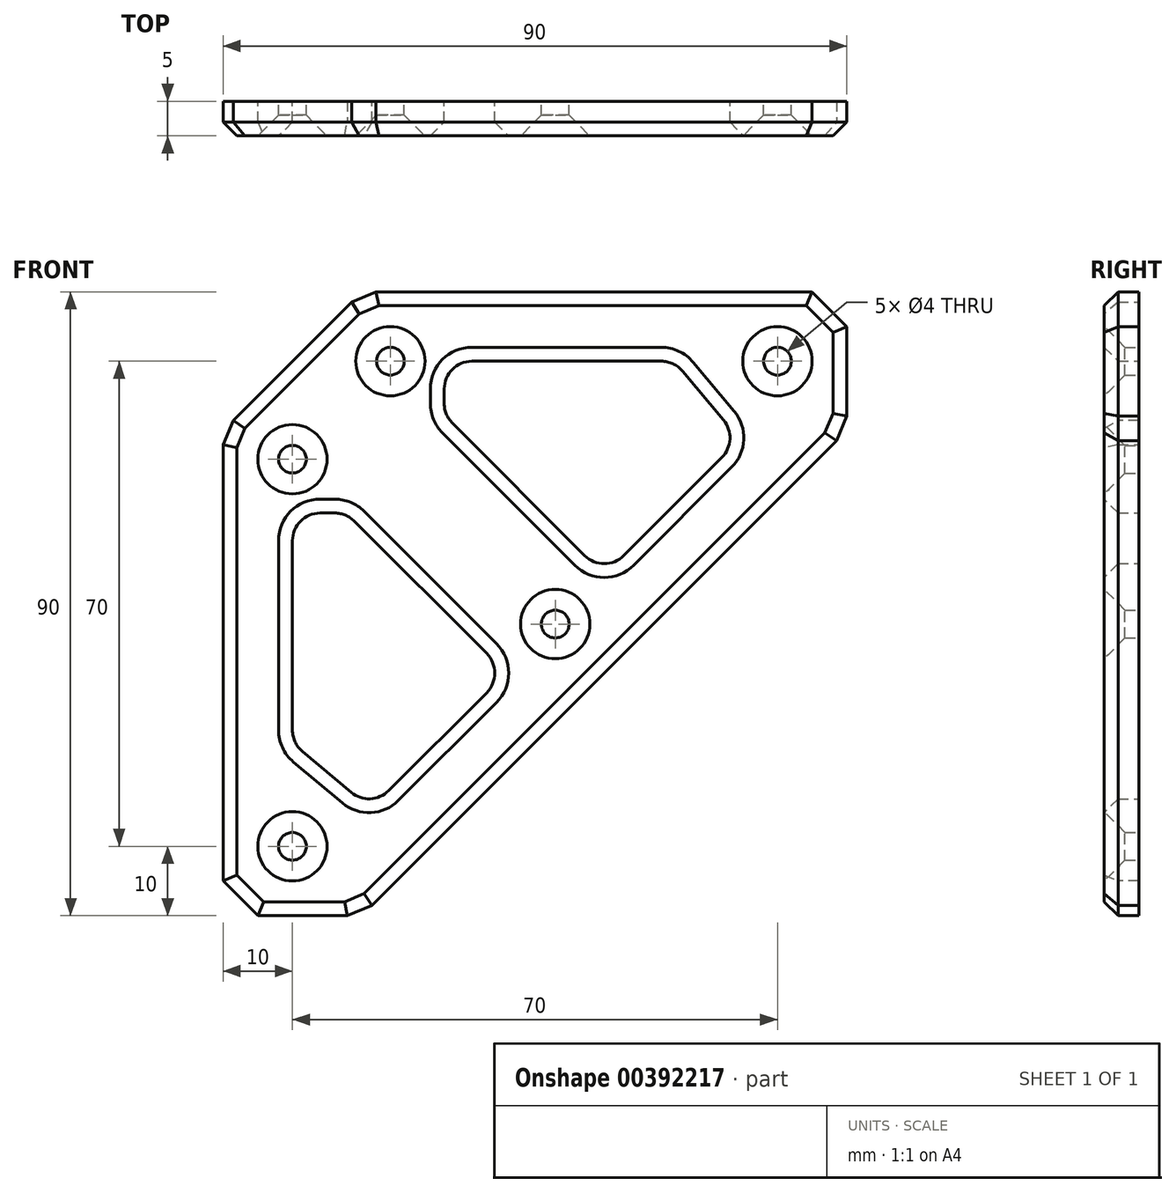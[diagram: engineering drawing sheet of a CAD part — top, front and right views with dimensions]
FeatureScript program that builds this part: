
annotation { "Feature Type Name" : "Feature", "Feature Type Description" : "" }
export const myFeature = defineFeature(function(context is Context, id is Id, definition is map)
    precondition{}
    {
        {
            var Q0;
            Q0=qCreatedBy(makeId("Front.planeOp"),FACE);
            var sketch = newSketch(context, id + "F0", { "sketchPlane" : qUnion([Q0])});
            skLineSegment(sketch, "E0", {"start": v(0, -20) * mm, "end": v(20, 0) * mm});
            skLineSegment(sketch, "E1", {"start": v(20, 0) * mm, "end": v(90, 0) * mm});
            skLineSegment(sketch, "E2", {"start": v(90, 0) * mm, "end": v(90, -20) * mm});
            skLineSegment(sketch, "E3", {"start": v(90, -20) * mm, "end": v(20, -90) * mm});
            skLineSegment(sketch, "E4", {"start": v(20, -90) * mm, "end": v(0, -90) * mm});
            skLineSegment(sketch, "E5", {"start": v(0, -90) * mm, "end": v(0, -20) * mm});
            skLineSegment(sketch, "E6.0", {"start": v(10, -24.14) * mm, "end": v(24.14, -10) * mm, "construction": true});
            skLineSegment(sketch, "E6.1", {"start": v(80, -10) * mm, "end": v(80, -15.86) * mm, "construction": true});
            skLineSegment(sketch, "E6.2", {"start": v(80, -15.86) * mm, "end": v(15.86, -80) * mm, "construction": true});
            skLineSegment(sketch, "E6.3", {"start": v(24.14, -10) * mm, "end": v(80, -10) * mm, "construction": true});
            skLineSegment(sketch, "E6.4", {"start": v(15.86, -80) * mm, "end": v(10, -80) * mm, "construction": true});
            skLineSegment(sketch, "E6.5", {"start": v(10, -80) * mm, "end": v(10, -24.14) * mm, "construction": true});
            skLineSegment(sketch, "E7", {"start": v(0, 0) * mm, "end": v(55, -55) * mm, "construction": true});
            skPoint(sketch, "E8", {"position": v(47.93, -47.93) * mm});
            skCircle(sketch, "E9", {"center": v(10, -24.14) * mm, "radius": 2 * mm});
            skCircle(sketch, "E10", {"center": v(24.14, -10) * mm, "radius": 2 * mm});
            skCircle(sketch, "E11", {"center": v(80, -10) * mm, "radius": 2 * mm});
            skCircle(sketch, "E12", {"center": v(47.93, -47.93) * mm, "radius": 2 * mm});
            skCircle(sketch, "E13", {"center": v(10, -80) * mm, "radius": 2 * mm});
            skLineSegment(sketch, "E14", {"start": v(66.28, -11.43) * mm, "end": v(72.2, -18.49) * mm});
            skLineSegment(sketch, "E15", {"start": v(71.97, -23.89) * mm, "end": v(57.83, -38.03) * mm});
            skLineSegment(sketch, "E16", {"start": v(52.17, -38.03) * mm, "end": v(33.08, -18.94) * mm});
            skLineSegment(sketch, "E17", {"start": v(31.9, -16.1) * mm, "end": v(31.9, -14) * mm});
            skLineSegment(sketch, "E18", {"start": v(35.9, -10) * mm, "end": v(63.22, -10) * mm});
            skPoint(sketch, "E19.visualSharp", {"position": v(55, -40.86) * mm});
            skArc(sketch, "E19.filletArc", {"start": v(52.17, -38.03) * mm, "mid": v(55, -39.2) * mm, "end": v(57.83, -38.03) * mm});
            skPoint(sketch, "E20.visualSharp", {"position": v(31.9, -17.77) * mm});
            skArc(sketch, "E20.filletArc", {"start": v(31.9, -16.1) * mm, "mid": v(32.21, -17.64) * mm, "end": v(33.08, -18.94) * mm});
            skPoint(sketch, "E21.visualSharp", {"position": v(31.9, -10) * mm});
            skArc(sketch, "E21.filletArc", {"start": v(35.9, -10) * mm, "mid": v(33.08, -11.17) * mm, "end": v(31.9, -14) * mm});
            skPoint(sketch, "E22.visualSharp", {"position": v(65.08, -10) * mm});
            skArc(sketch, "E22.filletArc", {"start": v(66.28, -11.43) * mm, "mid": v(64.9, -10.37) * mm, "end": v(63.22, -10) * mm});
            skPoint(sketch, "E23.visualSharp", {"position": v(74.56, -21.3) * mm});
            skArc(sketch, "E23.filletArc", {"start": v(71.97, -23.89) * mm, "mid": v(73.14, -21.23) * mm, "end": v(72.2, -18.49) * mm});
            skLineSegment(sketch, "E24.MirrorCS", {"start": v(16.1, -31.9) * mm, "end": v(14, -31.9) * mm});
            skArc(sketch, "E25.MirrorCS", {"start": v(16.1, -31.9) * mm, "mid": v(17.64, -32.21) * mm, "end": v(18.94, -33.08) * mm});
            skArc(sketch, "E26.MirrorCS", {"start": v(10, -35.9) * mm, "mid": v(11.17, -33.08) * mm, "end": v(14, -31.9) * mm});
            skPoint(sketch, "E27.MirrorP", {"position": v(17.77, -31.9) * mm});
            skPoint(sketch, "E28.MirrorP", {"position": v(10, -31.9) * mm});
            skPoint(sketch, "E29.MirrorP", {"position": v(40.86, -55) * mm});
            skArc(sketch, "E30.MirrorCS", {"start": v(38.03, -52.17) * mm, "mid": v(39.2, -55) * mm, "end": v(38.03, -57.83) * mm});
            skArc(sketch, "E31.MirrorCS", {"start": v(11.43, -66.28) * mm, "mid": v(10.37, -64.9) * mm, "end": v(10, -63.22) * mm});
            skPoint(sketch, "E32.MirrorP", {"position": v(10, -65.08) * mm});
            skArc(sketch, "E33.MirrorCS", {"start": v(23.89, -71.97) * mm, "mid": v(21.23, -73.14) * mm, "end": v(18.49, -72.2) * mm});
            skPoint(sketch, "E34.MirrorP", {"position": v(21.3, -74.56) * mm});
            skLineSegment(sketch, "E35.MirrorCS", {"start": v(11.43, -66.28) * mm, "end": v(18.49, -72.2) * mm});
            skLineSegment(sketch, "E36.MirrorCS", {"start": v(10, -35.9) * mm, "end": v(10, -63.22) * mm});
            skLineSegment(sketch, "E37.MirrorCS", {"start": v(38.03, -52.17) * mm, "end": v(18.94, -33.08) * mm});
            skLineSegment(sketch, "E38.MirrorCS", {"start": v(23.89, -71.97) * mm, "end": v(38.03, -57.83) * mm});
            skSolve(sketch);
        }
        {
            var Q0;
            Q0=qSketchRegion(id+"F0",true);
            extrude(context, id + "F1", {"entities" : qUnion([Q0]), "depth" : 5 * mm});
        }
        {
            var Q0;
            Q0=makeQuery(id+"F1.opExtrude","SWEPT_EDGE",EDGE,{"disambiguationData":[OSD([sQuery(id+"F0.wireOp",EDGE,"E1"),sQuery(id+"F0.wireOp",EDGE,"E2")])]});
            var Q1;
            Q1=makeQuery(id+"F1.opExtrude","SWEPT_EDGE",EDGE,{"disambiguationData":[OSD([sQuery(id+"F0.wireOp",EDGE,"E4"),sQuery(id+"F0.wireOp",EDGE,"E5")])]});
            var Q2;
            Q2=makeQuery(id+"F1.opExtrude","SWEPT_EDGE",EDGE,{"disambiguationData":[OSD([sQuery(id+"F0.wireOp",EDGE,"E0"),sQuery(id+"F0.wireOp",EDGE,"E5")])]});
            var Q3;
            Q3=makeQuery(id+"F1.opExtrude","SWEPT_EDGE",EDGE,{"disambiguationData":[OSD([sQuery(id+"F0.wireOp",EDGE,"E0"),sQuery(id+"F0.wireOp",EDGE,"E1")])]});
            var Q4;
            Q4=makeQuery(id+"F1.opExtrude","SWEPT_EDGE",EDGE,{"disambiguationData":[OSD([sQuery(id+"F0.wireOp",EDGE,"E2"),sQuery(id+"F0.wireOp",EDGE,"E3")])]});
            var Q5;
            Q5=makeQuery(id+"F1.opExtrude","SWEPT_EDGE",EDGE,{"disambiguationData":[OSD([sQuery(id+"F0.wireOp",EDGE,"E3"),sQuery(id+"F0.wireOp",EDGE,"E4")])]});
            chamfer(context, id + "F2", {"entities" : qUnion([Q0, Q1, Q2, Q3, Q4, Q5]), "width" : 5 * mm, "tangentPropagation" : true});
        }
        {
            var Q0;
            {var subQ0=sQuery(id+"F0.wireOp",EDGE,"E5");var subQ1=sQuery(id+"F0.wireOp",EDGE,"E0");Q0=makeQuery(id+"F2.opChamfer","BLEND_EDGE",EDGE,{"blendedFrom":[makeQuery(id+"F1.opExtrude","SWEPT_EDGE",EDGE,{"disambiguationData":[OSD([subQ1,subQ0])]}),makeQuery(id+"F1.opExtrude","CAP_FACE",FACE,{"disambiguationData":[OSD([subQ1,sQuery(id+"F0.wireOp",EDGE,"E1"),sQuery(id+"F0.wireOp",EDGE,"E2"),sQuery(id+"F0.wireOp",EDGE,"E3"),sQuery(id+"F0.wireOp",EDGE,"E4"),subQ0,sQuery(id+"F0.wireOp",EDGE,"E9"),sQuery(id+"F0.wireOp",EDGE,"E10"),sQuery(id+"F0.wireOp",EDGE,"E11"),sQuery(id+"F0.wireOp",EDGE,"E12"),sQuery(id+"F0.wireOp",EDGE,"E13")])],"isStart":false})],"blendedInto":[makeQuery(id+"F1.opExtrude","CAP_FACE",FACE,{"disambiguationData":[OSD([subQ1,sQuery(id+"F0.wireOp",EDGE,"E1"),sQuery(id+"F0.wireOp",EDGE,"E2"),sQuery(id+"F0.wireOp",EDGE,"E3"),sQuery(id+"F0.wireOp",EDGE,"E4"),subQ0,sQuery(id+"F0.wireOp",EDGE,"E9"),sQuery(id+"F0.wireOp",EDGE,"E10"),sQuery(id+"F0.wireOp",EDGE,"E11"),sQuery(id+"F0.wireOp",EDGE,"E12"),sQuery(id+"F0.wireOp",EDGE,"E13")])],"isStart":false})]});}
            var Q1;
            {var subQ0=sQuery(id+"F0.wireOp",EDGE,"E1");var subQ1=sQuery(id+"F0.wireOp",EDGE,"E0");Q1=makeQuery(id+"F2.opChamfer","BLEND_EDGE",EDGE,{"blendedFrom":[makeQuery(id+"F1.opExtrude","SWEPT_EDGE",EDGE,{"disambiguationData":[OSD([subQ1,subQ0])]}),makeQuery(id+"F1.opExtrude","CAP_FACE",FACE,{"disambiguationData":[OSD([subQ1,subQ0,sQuery(id+"F0.wireOp",EDGE,"E2"),sQuery(id+"F0.wireOp",EDGE,"E3"),sQuery(id+"F0.wireOp",EDGE,"E4"),sQuery(id+"F0.wireOp",EDGE,"E5"),sQuery(id+"F0.wireOp",EDGE,"E9"),sQuery(id+"F0.wireOp",EDGE,"E10"),sQuery(id+"F0.wireOp",EDGE,"E11"),sQuery(id+"F0.wireOp",EDGE,"E12"),sQuery(id+"F0.wireOp",EDGE,"E13")])],"isStart":false})],"blendedInto":[makeQuery(id+"F1.opExtrude","CAP_FACE",FACE,{"disambiguationData":[OSD([subQ1,subQ0,sQuery(id+"F0.wireOp",EDGE,"E2"),sQuery(id+"F0.wireOp",EDGE,"E3"),sQuery(id+"F0.wireOp",EDGE,"E4"),sQuery(id+"F0.wireOp",EDGE,"E5"),sQuery(id+"F0.wireOp",EDGE,"E9"),sQuery(id+"F0.wireOp",EDGE,"E10"),sQuery(id+"F0.wireOp",EDGE,"E11"),sQuery(id+"F0.wireOp",EDGE,"E12"),sQuery(id+"F0.wireOp",EDGE,"E13")])],"isStart":false})]});}
            var Q2;
            Q2=makeQuery(id+"F1.opExtrude","CAP_EDGE",EDGE,{"disambiguationData":[OSD([sQuery(id+"F0.wireOp",EDGE,"E0")])],"isStart":false});
            var Q3;
            {var subQ0=sQuery(id+"F0.wireOp",EDGE,"E2");var subQ1=sQuery(id+"F0.wireOp",EDGE,"E1");Q3=makeQuery(id+"F2.opChamfer","BLEND_EDGE",EDGE,{"blendedFrom":[makeQuery(id+"F1.opExtrude","SWEPT_EDGE",EDGE,{"disambiguationData":[OSD([subQ1,subQ0])]}),makeQuery(id+"F1.opExtrude","CAP_FACE",FACE,{"disambiguationData":[OSD([sQuery(id+"F0.wireOp",EDGE,"E0"),subQ1,subQ0,sQuery(id+"F0.wireOp",EDGE,"E3"),sQuery(id+"F0.wireOp",EDGE,"E4"),sQuery(id+"F0.wireOp",EDGE,"E5"),sQuery(id+"F0.wireOp",EDGE,"E9"),sQuery(id+"F0.wireOp",EDGE,"E10"),sQuery(id+"F0.wireOp",EDGE,"E11"),sQuery(id+"F0.wireOp",EDGE,"E12"),sQuery(id+"F0.wireOp",EDGE,"E13")])],"isStart":false})],"blendedInto":[makeQuery(id+"F1.opExtrude","CAP_FACE",FACE,{"disambiguationData":[OSD([sQuery(id+"F0.wireOp",EDGE,"E0"),subQ1,subQ0,sQuery(id+"F0.wireOp",EDGE,"E3"),sQuery(id+"F0.wireOp",EDGE,"E4"),sQuery(id+"F0.wireOp",EDGE,"E5"),sQuery(id+"F0.wireOp",EDGE,"E9"),sQuery(id+"F0.wireOp",EDGE,"E10"),sQuery(id+"F0.wireOp",EDGE,"E11"),sQuery(id+"F0.wireOp",EDGE,"E12"),sQuery(id+"F0.wireOp",EDGE,"E13")])],"isStart":false})]});}
            var Q4;
            {var subQ0=sQuery(id+"F0.wireOp",EDGE,"E3");var subQ1=sQuery(id+"F0.wireOp",EDGE,"E2");Q4=makeQuery(id+"F2.opChamfer","BLEND_EDGE",EDGE,{"blendedFrom":[makeQuery(id+"F1.opExtrude","SWEPT_EDGE",EDGE,{"disambiguationData":[OSD([subQ1,subQ0])]}),makeQuery(id+"F1.opExtrude","CAP_FACE",FACE,{"disambiguationData":[OSD([sQuery(id+"F0.wireOp",EDGE,"E0"),sQuery(id+"F0.wireOp",EDGE,"E1"),subQ1,subQ0,sQuery(id+"F0.wireOp",EDGE,"E4"),sQuery(id+"F0.wireOp",EDGE,"E5"),sQuery(id+"F0.wireOp",EDGE,"E9"),sQuery(id+"F0.wireOp",EDGE,"E10"),sQuery(id+"F0.wireOp",EDGE,"E11"),sQuery(id+"F0.wireOp",EDGE,"E12"),sQuery(id+"F0.wireOp",EDGE,"E13")])],"isStart":false})],"blendedInto":[makeQuery(id+"F1.opExtrude","CAP_FACE",FACE,{"disambiguationData":[OSD([sQuery(id+"F0.wireOp",EDGE,"E0"),sQuery(id+"F0.wireOp",EDGE,"E1"),subQ1,subQ0,sQuery(id+"F0.wireOp",EDGE,"E4"),sQuery(id+"F0.wireOp",EDGE,"E5"),sQuery(id+"F0.wireOp",EDGE,"E9"),sQuery(id+"F0.wireOp",EDGE,"E10"),sQuery(id+"F0.wireOp",EDGE,"E11"),sQuery(id+"F0.wireOp",EDGE,"E12"),sQuery(id+"F0.wireOp",EDGE,"E13")])],"isStart":false})]});}
            var Q5;
            Q5=makeQuery(id+"F1.opExtrude","CAP_EDGE",EDGE,{"disambiguationData":[OSD([sQuery(id+"F0.wireOp",EDGE,"E2")])],"isStart":false});
            var Q6;
            Q6=makeQuery(id+"F1.opExtrude","CAP_EDGE",EDGE,{"disambiguationData":[OSD([sQuery(id+"F0.wireOp",EDGE,"E1")])],"isStart":false});
            var Q7;
            {var subQ0=sQuery(id+"F0.wireOp",EDGE,"E4");var subQ1=sQuery(id+"F0.wireOp",EDGE,"E3");Q7=makeQuery(id+"F2.opChamfer","BLEND_EDGE",EDGE,{"blendedFrom":[makeQuery(id+"F1.opExtrude","SWEPT_EDGE",EDGE,{"disambiguationData":[OSD([subQ1,subQ0])]}),makeQuery(id+"F1.opExtrude","CAP_FACE",FACE,{"disambiguationData":[OSD([sQuery(id+"F0.wireOp",EDGE,"E0"),sQuery(id+"F0.wireOp",EDGE,"E1"),sQuery(id+"F0.wireOp",EDGE,"E2"),subQ1,subQ0,sQuery(id+"F0.wireOp",EDGE,"E5"),sQuery(id+"F0.wireOp",EDGE,"E9"),sQuery(id+"F0.wireOp",EDGE,"E10"),sQuery(id+"F0.wireOp",EDGE,"E11"),sQuery(id+"F0.wireOp",EDGE,"E12"),sQuery(id+"F0.wireOp",EDGE,"E13")])],"isStart":false})],"blendedInto":[makeQuery(id+"F1.opExtrude","CAP_FACE",FACE,{"disambiguationData":[OSD([sQuery(id+"F0.wireOp",EDGE,"E0"),sQuery(id+"F0.wireOp",EDGE,"E1"),sQuery(id+"F0.wireOp",EDGE,"E2"),subQ1,subQ0,sQuery(id+"F0.wireOp",EDGE,"E5"),sQuery(id+"F0.wireOp",EDGE,"E9"),sQuery(id+"F0.wireOp",EDGE,"E10"),sQuery(id+"F0.wireOp",EDGE,"E11"),sQuery(id+"F0.wireOp",EDGE,"E12"),sQuery(id+"F0.wireOp",EDGE,"E13")])],"isStart":false})]});}
            var Q8;
            {var subQ0=sQuery(id+"F0.wireOp",EDGE,"E5");var subQ1=sQuery(id+"F0.wireOp",EDGE,"E4");Q8=makeQuery(id+"F2.opChamfer","BLEND_EDGE",EDGE,{"blendedFrom":[makeQuery(id+"F1.opExtrude","SWEPT_EDGE",EDGE,{"disambiguationData":[OSD([subQ1,subQ0])]}),makeQuery(id+"F1.opExtrude","CAP_FACE",FACE,{"disambiguationData":[OSD([sQuery(id+"F0.wireOp",EDGE,"E0"),sQuery(id+"F0.wireOp",EDGE,"E1"),sQuery(id+"F0.wireOp",EDGE,"E2"),sQuery(id+"F0.wireOp",EDGE,"E3"),subQ1,subQ0,sQuery(id+"F0.wireOp",EDGE,"E9"),sQuery(id+"F0.wireOp",EDGE,"E10"),sQuery(id+"F0.wireOp",EDGE,"E11"),sQuery(id+"F0.wireOp",EDGE,"E12"),sQuery(id+"F0.wireOp",EDGE,"E13")])],"isStart":false})],"blendedInto":[makeQuery(id+"F1.opExtrude","CAP_FACE",FACE,{"disambiguationData":[OSD([sQuery(id+"F0.wireOp",EDGE,"E0"),sQuery(id+"F0.wireOp",EDGE,"E1"),sQuery(id+"F0.wireOp",EDGE,"E2"),sQuery(id+"F0.wireOp",EDGE,"E3"),subQ1,subQ0,sQuery(id+"F0.wireOp",EDGE,"E9"),sQuery(id+"F0.wireOp",EDGE,"E10"),sQuery(id+"F0.wireOp",EDGE,"E11"),sQuery(id+"F0.wireOp",EDGE,"E12"),sQuery(id+"F0.wireOp",EDGE,"E13")])],"isStart":false})]});}
            var Q9;
            Q9=makeQuery(id+"F1.opExtrude","CAP_EDGE",EDGE,{"disambiguationData":[OSD([sQuery(id+"F0.wireOp",EDGE,"E4")])],"isStart":false});
            var Q10;
            Q10=makeQuery(id+"F1.opExtrude","CAP_EDGE",EDGE,{"disambiguationData":[OSD([sQuery(id+"F0.wireOp",EDGE,"E5")])],"isStart":false});
            var Q11;
            Q11=makeQuery(id+"F1.opExtrude","CAP_EDGE",EDGE,{"disambiguationData":[OSD([sQuery(id+"F0.wireOp",EDGE,"E3")])],"isStart":false});
            chamfer(context, id + "F3", {"entities" : qUnion([Q0, Q1, Q2, Q3, Q4, Q5, Q6, Q7, Q8, Q9, Q10, Q11]), "width" : 2 * mm, "tangentPropagation" : true});
        }
        {
            var Q0;
            Q0=makeQuery(id+"F1.opExtrude","CAP_EDGE",EDGE,{"disambiguationData":[OSD([sQuery(id+"F0.wireOp",EDGE,"E9")])],"isStart":false});
            var Q1;
            Q1=makeQuery(id+"F1.opExtrude","CAP_EDGE",EDGE,{"disambiguationData":[OSD([sQuery(id+"F0.wireOp",EDGE,"E10")])],"isStart":false});
            var Q2;
            Q2=makeQuery(id+"F1.opExtrude","CAP_EDGE",EDGE,{"disambiguationData":[OSD([sQuery(id+"F0.wireOp",EDGE,"E11")])],"isStart":false});
            var Q3;
            Q3=makeQuery(id+"F1.opExtrude","CAP_EDGE",EDGE,{"disambiguationData":[OSD([sQuery(id+"F0.wireOp",EDGE,"E12")])],"isStart":false});
            var Q4;
            Q4=makeQuery(id+"F1.opExtrude","CAP_EDGE",EDGE,{"disambiguationData":[OSD([sQuery(id+"F0.wireOp",EDGE,"E13")])],"isStart":false});
            chamfer(context, id + "F4", {"entities" : qUnion([Q0, Q1, Q2, Q3, Q4]), "width" : 3 * mm, "tangentPropagation" : true});
        }
        {
            var Q0;
            Q0=makeQuery(id+"F1.opExtrude","CAP_EDGE",EDGE,{"disambiguationData":[OSD([sQuery(id+"F0.wireOp",EDGE,"E38.MirrorCS")])],"isStart":false});
            var Q1;
            Q1=makeQuery(id+"F1.opExtrude","CAP_EDGE",EDGE,{"disambiguationData":[OSD([sQuery(id+"F0.wireOp",EDGE,"E33.MirrorCS")])],"isStart":false});
            var Q2;
            Q2=makeQuery(id+"F1.opExtrude","CAP_EDGE",EDGE,{"disambiguationData":[OSD([sQuery(id+"F0.wireOp",EDGE,"E35.MirrorCS")])],"isStart":false});
            var Q3;
            Q3=makeQuery(id+"F1.opExtrude","CAP_EDGE",EDGE,{"disambiguationData":[OSD([sQuery(id+"F0.wireOp",EDGE,"E31.MirrorCS")])],"isStart":false});
            var Q4;
            Q4=makeQuery(id+"F1.opExtrude","CAP_EDGE",EDGE,{"disambiguationData":[OSD([sQuery(id+"F0.wireOp",EDGE,"E36.MirrorCS")])],"isStart":false});
            var Q5;
            Q5=makeQuery(id+"F1.opExtrude","CAP_EDGE",EDGE,{"disambiguationData":[OSD([sQuery(id+"F0.wireOp",EDGE,"E26.MirrorCS")])],"isStart":false});
            var Q6;
            Q6=makeQuery(id+"F1.opExtrude","CAP_EDGE",EDGE,{"disambiguationData":[OSD([sQuery(id+"F0.wireOp",EDGE,"E25.MirrorCS")])],"isStart":false});
            var Q7;
            Q7=makeQuery(id+"F1.opExtrude","SWEPT_EDGE",EDGE,{"disambiguationData":[OSD([sQuery(id+"F0.wireOp",EDGE,"E24.MirrorCS"),sQuery(id+"F0.wireOp",EDGE,"E26.MirrorCS")])]});
            var Q8;
            Q8=makeQuery(id+"F1.opExtrude","CAP_EDGE",EDGE,{"disambiguationData":[OSD([sQuery(id+"F0.wireOp",EDGE,"E24.MirrorCS")])],"isStart":false});
            var Q9;
            Q9=makeQuery(id+"F1.opExtrude","CAP_EDGE",EDGE,{"disambiguationData":[OSD([sQuery(id+"F0.wireOp",EDGE,"E37.MirrorCS")])],"isStart":false});
            var Q10;
            Q10=makeQuery(id+"F1.opExtrude","CAP_EDGE",EDGE,{"disambiguationData":[OSD([sQuery(id+"F0.wireOp",EDGE,"E30.MirrorCS")])],"isStart":false});
            var Q11;
            Q11=makeQuery(id+"F1.opExtrude","CAP_EDGE",EDGE,{"disambiguationData":[OSD([sQuery(id+"F0.wireOp",EDGE,"E16")])],"isStart":false});
            chamfer(context, id + "F5", {"entities" : qUnion([Q0, Q1, Q2, Q3, Q4, Q5, Q6, Q7, Q8, Q9, Q10, Q11]), "width" : 2 * mm, "tangentPropagation" : true});
        }
    });
